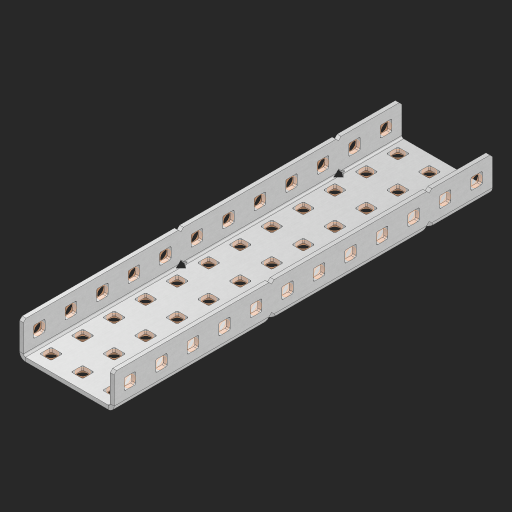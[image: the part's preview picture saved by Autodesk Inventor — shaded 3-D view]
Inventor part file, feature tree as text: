
AUTODESK INVENTOR PART (.ipt)
format: ipt  version: 2023 (Build 270158000, 158)  size: 1,010,176 bytes
history: native  units: in
note: dims shown in document units (in); Inventor stores cm internally (conversion verified against a paired STEP export)
features: other x65, extrude x59, sheet_metal_op x10, sketch x8, mirror x1, pattern_linear x1, chamfer x1
ambient origin geometry x8: Origin, YZ Plane, XZ Plane, XY Plane, X Axis, Y Axis, Z Axis, Center Point
bodies: Solid1 (feature_tree), Body (feature_tree)
feature tree (145):
  other  "Flange Pattern Plane"
  sheet_metal_op  "Flange Pattern"
  sheet_metal_op  "Body Pattern"
  other  "Arc Length"
  mirror  "Notch Mirror"
  pattern_linear  "Notch Pattern"  Spacing1=0.25in  [1 undecoded]
  chamfer  "End Chamfer"
  extrude  "Half Cut"  Depth=0.0625in
  sketch  "Sketch1"  dims[d0=1.5in]
  other  "Plate1"
  sketch  "Sketch2"  dims[d1=6.0in]
  other  "Plate2"
  sheet_metal_op  "Bend1"
  sheet_metal_op  "Corner1"
  sketch  "Sketch3"  dims[d2=0.0625in]
  other  "Flange Pattern Sketch"
  sketch  "Sketch7"  dims[d3=0.0625in]
  other  "Srf1"
  other  "Srf2"
  sketch  "Sketch8"  dims[d4=0.0312in]
  sketch  "Sketch9"  dims[d5=0.125in]
  other  "Srf91"
  sheet_metal_op  "Body Pattern Sketch"
  other  "Srf92"
  sketch  "Sketch13"  dims[d6=0.0625in]
  sketch  "Sketch14"  dims[d7=0.5in d8=90.0deg d9=0.0312in d10=0.25in d11=0.0625in d12=0.0625in d16=0.182in d17=0.02in d18=0.0625in d19=0.0in d20=0.25in d21=0.25in d46=0.172in d47=1.0in d48=0.0in d49=0.182in d50=0.02in d51=0.25in d52=0.25in d53=0.0625in d54=0.0in d55=0.172in d56=1.0in d57=0.0in d60=4.7244in d62=0.5in d63=1.1811in d65=0.5in d85=0.1473in d86=0.1782in d88=0.04in d89=0.0625in d90=0.0in d91=0.04in d92=0.0491in d95=2.5in d96=0.04in d97=0.25in d98=45.0deg d101=0.0in d102=2.497in d131=1.5in d132=4.7244in d134=0.5in d139=0.5in]
  other  "Srf856"
  other  "Srf1310"
  other  "Srf1311"
  other  "Srf1312"
  other  "Srf1376"
  other  "Srf1377"
  other  "Srf1728"
  other  "Srf1755"
  other  "Srf1878"
  other  "Srf1879"
  other  "Srf1880"
  other  "Srf1881"
  other  "Srf1882"
  other  "Srf1883"
  other  "Srf1884"
  other  "Srf1885"
  other  "Srf1886"
  other  "Srf1887"
  other  "Srf1888"
  other  "Srf1889"
  other  "Srf1890"
  other  "Srf1891"
  other  "Srf1892"
  other  "Srf1893"
  other  "Srf1894"
  other  "Srf1895"
  other  "Srf1942"
  other  "Srf1943"
  other  "Srf1944"
  other  "Srf1945"
  other  "Srf1946"
  other  "Srf1947"
  other  "Srf1948"
  other  "Srf1949"
  other  "Srf1950"
  other  "Srf1951"
  other  "Srf1952"
  other  "Srf1953"
  other  "Srf1954"
  other  "Srf1955"
  other  "Srf1956"
  other  "Srf1957"
  other  "Srf1958"
  other  "Srf1959"
  other  "Srf1960"
  other  "Srf1961"
  other  "Srf1962"
  other  "Srf1963"
  other  "Srf1964"
  other  "Srf1965"
  other  "Srf1966"
  other  "Srf1967"
  other  "Srf1968"
  other  "Srf1969"
  other  "Srf1970"
  other  "Srf1971"
  sheet_metal_op  "Flange Stamp"
  sheet_metal_op  "Flange Circle"
  sheet_metal_op  "Body Stamp"
  sheet_metal_op  "Body Circle"
  sheet_metal_op  "Notch"
  extrude  "ExtrusionSrf2"  Depth=0.0625in
  extrude  "ExtrusionSrf92"  Depth=1.5in
  extrude  "ExtrusionSrf856"  Depth=0.02in
  extrude  "ExtrusionSrf1310"  Depth=0.0625in
  extrude  "ExtrusionSrf1311"  TaperAngle=0.0deg  [1 undecoded]
  extrude  "ExtrusionSrf1312"  Depth=0.25in
  extrude  "ExtrusionSrf1376"  Depth=0.25in
  extrude  "ExtrusionSrf1377"  Depth=1.5in
  extrude  "ExtrusionSrf1728"  Depth=1.5in TaperAngle=0.0deg
  extrude  "ExtrusionSrf1755"  Depth=1.5in
  extrude  "ExtrusionSrf1878"  Depth=0.02in
  extrude  "ExtrusionSrf1879"  Depth=0.25in
  extrude  "ExtrusionSrf1880"  Depth=0.25in
  extrude  "ExtrusionSrf1881"  Depth=0.0625in
  extrude  "ExtrusionSrf1882"  TaperAngle=0.0deg  [1 undecoded]
  extrude  "ExtrusionSrf1883"  Depth=1.5in
  extrude  "ExtrusionSrf1884"  Depth=1.5in TaperAngle=0.0deg
  extrude  "ExtrusionSrf1885"  Depth=1.5in
  extrude  "ExtrusionSrf1886"  Depth=1.5in
  extrude  "ExtrusionSrf1887"  Depth=1.5in
  extrude  "ExtrusionSrf1888"  Depth=1.5in
  extrude  "ExtrusionSrf1889"  Depth=1.5in
  extrude  "ExtrusionSrf1890"  Depth=0.0625in
  extrude  "ExtrusionSrf1891"  TaperAngle=0.0deg  [1 undecoded]
  extrude  "ExtrusionSrf1892"  Depth=1.5in
  extrude  "ExtrusionSrf1893"  Depth=1.5in
  extrude  "ExtrusionSrf1894"  Depth=1.5in
  extrude  "ExtrusionSrf1895"  Depth=0.25in TaperAngle=45.0deg
  extrude  "ExtrusionSrf1942"  TaperAngle=0.0deg  [1 undecoded]
  extrude  "ExtrusionSrf1943"  Depth=1.5in
  extrude  "ExtrusionSrf1944"  Depth=1.5in
  extrude  "ExtrusionSrf1945"  Depth=1.5in
  extrude  "ExtrusionSrf1946"  Depth=1.5in
  extrude  "ExtrusionSrf1947"  Depth=1.5in
  extrude  "ExtrusionSrf1948"  [1 undecoded]
  extrude  "ExtrusionSrf1949"  [1 undecoded]
  extrude  "ExtrusionSrf1950"  [1 undecoded]
  extrude  "ExtrusionSrf1951"  [1 undecoded]
  extrude  "ExtrusionSrf1952"  [1 undecoded]
  extrude  "ExtrusionSrf1953"  [1 undecoded]
  extrude  "ExtrusionSrf1954"  [1 undecoded]
  extrude  "ExtrusionSrf1955"  [1 undecoded]
  extrude  "ExtrusionSrf1956"  [1 undecoded]
  extrude  "ExtrusionSrf1957"  [1 undecoded]
  extrude  "ExtrusionSrf1958"  [1 undecoded]
  extrude  "ExtrusionSrf1959"  [1 undecoded]
  extrude  "ExtrusionSrf1960"  [1 undecoded]
  extrude  "ExtrusionSrf1961"  [1 undecoded]
  extrude  "ExtrusionSrf1962"  [1 undecoded]
  extrude  "ExtrusionSrf1963"  [1 undecoded]
  extrude  "ExtrusionSrf1964"  [1 undecoded]
  extrude  "ExtrusionSrf1965"  [1 undecoded]
  extrude  "ExtrusionSrf1966"  [1 undecoded]
  extrude  "ExtrusionSrf1967"  [1 undecoded]
  extrude  "ExtrusionSrf1968"  [1 undecoded]
  extrude  "ExtrusionSrf1969"  [1 undecoded]
  extrude  "ExtrusionSrf1970"  [1 undecoded]
  extrude  "ExtrusionSrf1971"  [1 undecoded]
note: 29 required parameter values undecoded (feature->parameter linkage not recoverable at this tier; creation-order binding heuristic only, values carry confidence <= 0.55)
